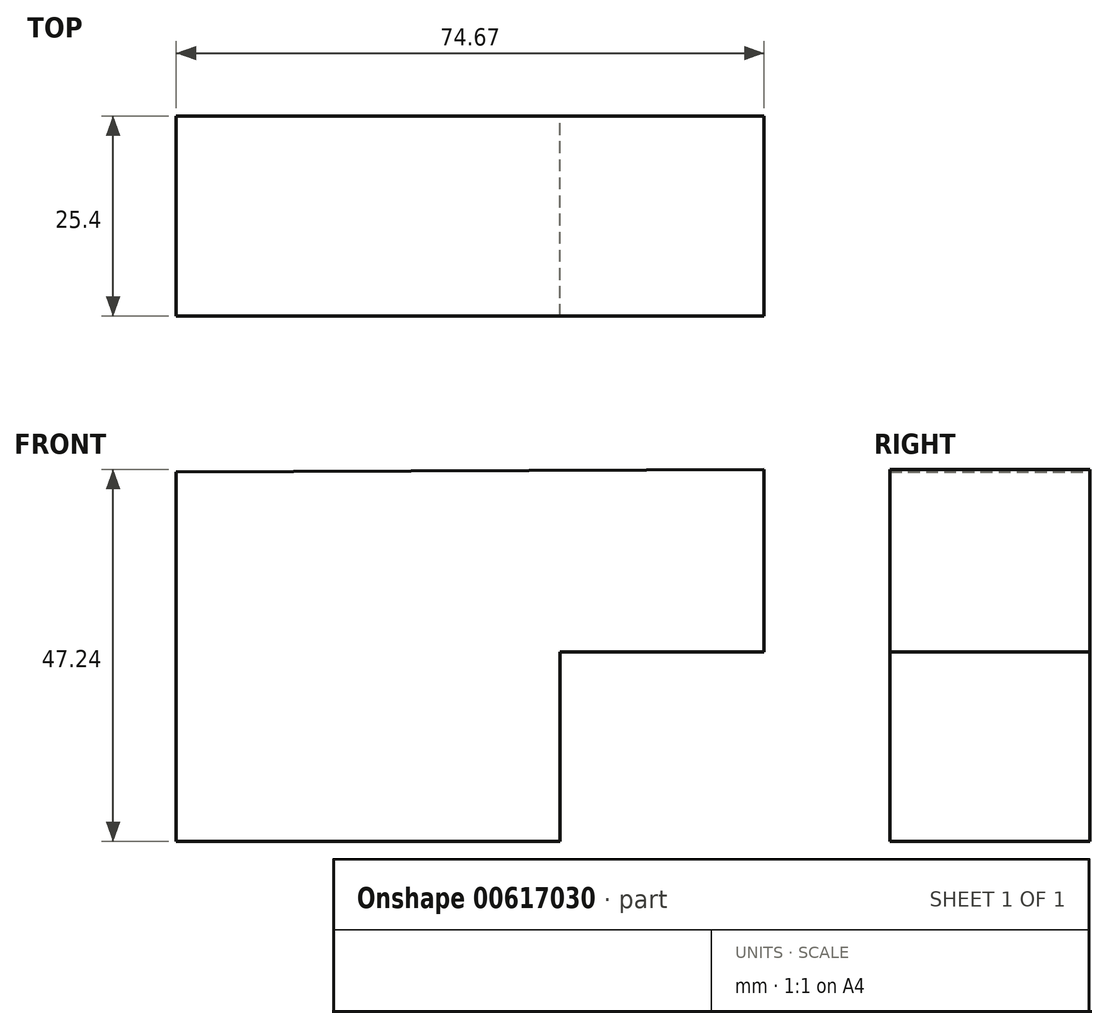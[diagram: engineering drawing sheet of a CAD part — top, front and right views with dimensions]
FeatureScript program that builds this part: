
annotation { "Feature Type Name" : "Feature", "Feature Type Description" : "" }
export const myFeature = defineFeature(function(context is Context, id is Id, definition is map)
    precondition{}
    {
        {
            var Q0;
            Q0=qCreatedBy(makeId("Front.planeOp"),FACE);
            var sketch = newSketch(context, id + "F0", { "sketchPlane" : qUnion([Q0])});
            skLineSegment(sketch, "E0", {"start": v(-24.23, 22.86) * mm, "end": v(-24.23, -24.08) * mm});
            skLineSegment(sketch, "E1", {"start": v(24.54, -24.08) * mm, "end": v(-24.23, -24.08) * mm});
            skLineSegment(sketch, "E2", {"start": v(24.54, -24.08) * mm, "end": v(24.54, 0) * mm});
            skLineSegment(sketch, "E3", {"start": v(-24.23, 22.86) * mm, "end": v(50.44, 23.16) * mm});
            skLineSegment(sketch, "E4", {"start": v(50.44, 23.16) * mm, "end": v(50.44, 0) * mm});
            skLineSegment(sketch, "E5", {"start": v(50.44, 0) * mm, "end": v(24.54, 0) * mm});
            skSolve(sketch);
        }
        {
            var Q0;
            Q0 = qSketchRegion(id + "F0", true);
            extrude(context, id + "F1", {"entities" : qUnion([Q0]), "depth" : 25.4 * mm, "offsetDistance" : 25.4 * mm});
        }
    });
